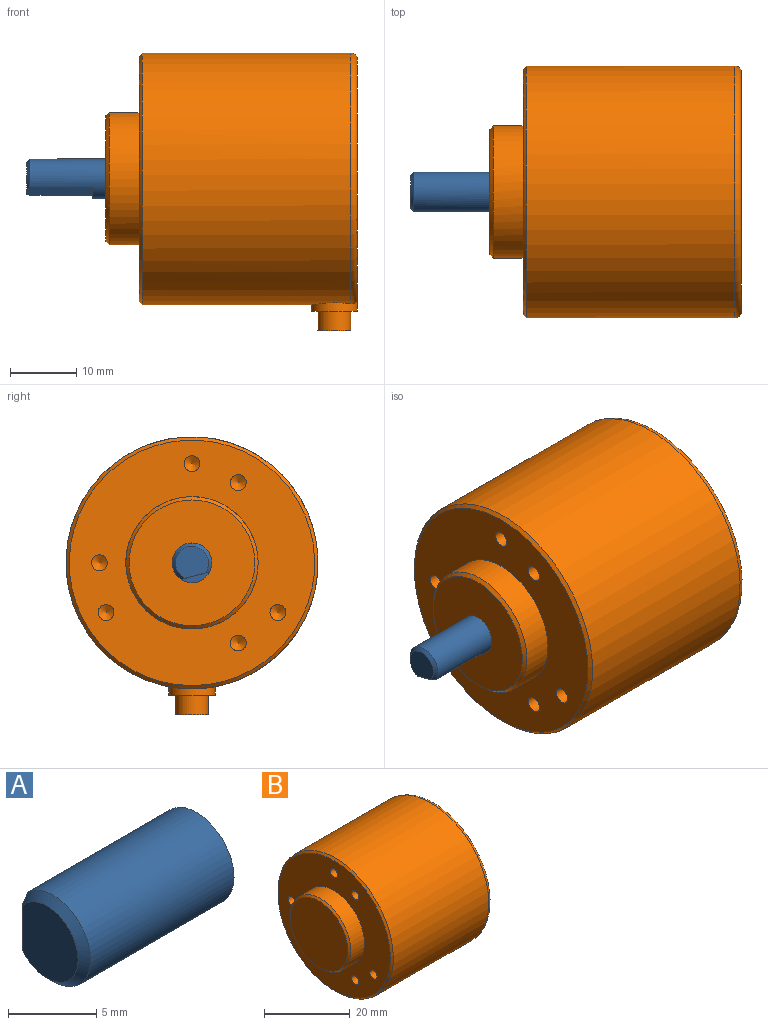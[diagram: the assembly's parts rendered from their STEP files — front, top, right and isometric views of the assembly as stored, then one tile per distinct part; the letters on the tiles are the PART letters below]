
ASSEMBLY  parts=2 mates=1
PART A: 6 faces, bbox 12x6x6 mm
  f0: plane 5x4.5mm, normal (-1,0,0), area 18.6mm2, adj f3,f5
  f1: cylinder r=3mm len=11.5mm, axis (1,0,0), area 168.8mm2, adj f2,f3,f4,f5
  f2: plane 6x6mm, normal (1,0,0), area 28.3mm2, adj f1
  f3: plane 10x4.47mm, normal (0,1,0), area 44.4mm2, adj f0,f1,f4,f5
  f4: plane 4.47x1mm, normal (-1,0,0), area 3.1mm2, adj f1,f3
  f5: cone r=2.5mm half-angle=45deg, axis (1,0,0), area 9.3mm2, adj f0,f1,f3
PART B: 24 faces, bbox 38x41.2x43.6 mm
  f0: cylinder r=19.05mm len=38.1mm, axis (-1,0,0), area 3737.5mm2, adj f18,f19,f20
  f1: plane 36.1x36.1mm, normal (1,0,0), area 1023.5mm2, adj f19
  f2: plane 37.1x37.1mm, normal (-1,0,0), area 739.7mm2, adj f3,f5,f7,f9,f11,f13,f15,f18
  f3: cylinder r=10mm len=20mm, axis (1,0,0), area 282.7mm2, adj f2,f17
  f4: plane 19x19mm, normal (-1,0,0), area 283.5mm2, adj f17
  f5: cylinder r=1.2mm len=6mm, axis (-1,0,0), area 45.2mm2, adj f2,f6
  f6: cone r=0mm half-angle=59deg, axis (-1,0,0), area 5.3mm2, adj f5
  f7: cylinder r=1.2mm len=6mm, axis (-1,0,0), area 45.2mm2, adj f2,f8
  f8: cone r=0mm half-angle=59deg, axis (-1,0,0), area 5.3mm2, adj f7
  f9: cylinder r=1.2mm len=6mm, axis (-1,0,0), area 45.2mm2, adj f2,f10
  f10: cone r=0mm half-angle=59deg, axis (-1,0,0), area 5.3mm2, adj f9
  f11: cylinder r=1.2mm len=6mm, axis (-1,0,0), area 45.2mm2, adj f2,f12
  f12: cone r=0mm half-angle=59deg, axis (-1,0,0), area 5.3mm2, adj f11
  f13: cylinder r=1.2mm len=6mm, axis (-1,0,0), area 45.2mm2, adj f2,f14
  f14: cone r=0mm half-angle=59deg, axis (-1,0,0), area 5.3mm2, adj f13
  f15: cylinder r=1.2mm len=6mm, axis (-1,0,0), area 45.2mm2, adj f2,f16
  f16: cone r=0mm half-angle=59deg, axis (-1,0,0), area 5.3mm2, adj f15
  f17: cone r=9.5mm half-angle=45deg, axis (1,0,0), area 43.3mm2, adj f3,f4
  f18: cone r=19.05mm half-angle=45deg, axis (1,0,0), area 83.5mm2, adj f0,f2
  f19: torus R=18.05mm, axis (1,0,0), area 180.2mm2, adj f0,f1,f20
  f20: cylinder r=3.5mm len=7mm, axis (0,0,1), area 26.5mm2, adj f0,f19,f21
  f21: plane 7x7mm, normal (0,0,-1), area 18.8mm2, adj f20,f22
  f22: cylinder r=2.5mm len=5mm, axis (0,0,1), area 47.1mm2, adj f21,f23
  f23: plane 5x5mm, normal (0,0,-1), area 19.6mm2, adj f22
PLACE A rot(axis=(-1,0,0),104.6deg) t=(0,0,0)mm
PLACE B at identity fixed
MATE revolute A.f1 <-> B.f0  axis (1,0,0) through (-5,0,0)mm
